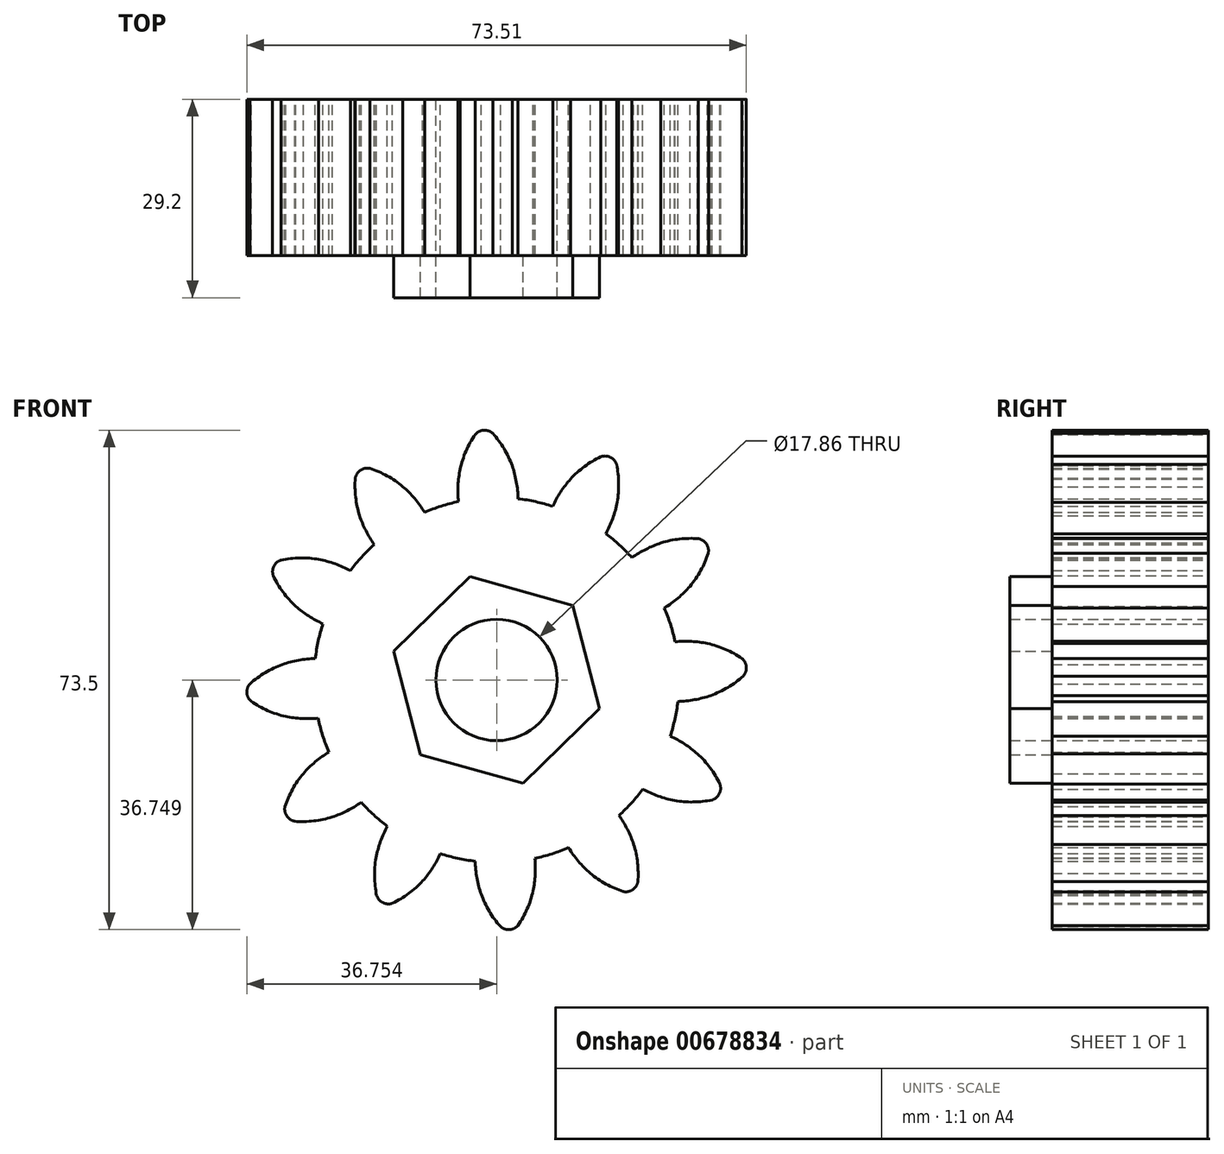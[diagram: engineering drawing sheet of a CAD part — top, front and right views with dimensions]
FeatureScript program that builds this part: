
annotation { "Feature Type Name" : "Feature", "Feature Type Description" : "" }
export const myFeature = defineFeature(function(context is Context, id is Id, definition is map)
    precondition{}
    {
        {
            var Q0;
            Q0=qCreatedBy(makeId("Front.planeOp"),FACE);
            var sketch = newSketch(context, id + "F0", { "sketchPlane" : qUnion([Q0])});
            skCircle(sketch, "E0", {"center": v(4.2, 11.54) * mm, "radius": 26.86 * mm});
            skCircle(sketch, "E1", {"center": v(4.2, 11.54) * mm, "radius": 29.34 * mm, "construction": true});
            skCircle(sketch, "E2", {"center": v(4.2, 11.54) * mm, "radius": 31.75 * mm, "construction": true});
            skLineSegment(sketch, "E3", {"start": v(4.2, 11.54) * mm, "end": v(4.2, 64.57) * mm, "construction": true});
            skLineSegment(sketch, "E4", {"start": v(4.2, 11.54) * mm, "end": v(-2.1, 107.57) * mm, "construction": true});
            skCircle(sketch, "E5", {"center": v(4.2, 11.54) * mm, "radius": 27.57 * mm, "construction": true});
            skLineSegment(sketch, "E6", {"start": v(4.2, 40.88) * mm, "end": v(-62.18, 40.88) * mm, "construction": true});
            skLineSegment(sketch, "E7", {"start": v(4.2, 40.88) * mm, "end": v(-57.88, 18.28) * mm, "construction": true});
            skCircle(sketch, "E8", {"center": v(4.2, 40.88) * mm, "radius": 14.6 * mm, "construction": true});
            skCircle(sketch, "E9", {"center": v(-9.53, 35.88) * mm, "radius": 14.6 * mm, "construction": true});
            skArc(sketch, "E10", {"start": v(6.48, 43.07) * mm, "mid": v(5.28, 45.59) * mm, "end": v(3.62, 47.83) * mm});
            skArc(sketch, "E11", {"start": v(7.36, 38.11) * mm, "mid": v(7.11, 40.63) * mm, "end": v(6.48, 43.07) * mm});
            skArc(sketch, "E12.MirrorCS", {"start": v(-1.18, 42.57) * mm, "mid": v(-0.31, 45.22) * mm, "end": v(1.03, 47.67) * mm});
            skArc(sketch, "E13.MirrorCS", {"start": v(-1.4, 37.54) * mm, "mid": v(-1.49, 40.06) * mm, "end": v(-1.18, 42.57) * mm});
            skArc(sketch, "E14", {"start": v(3.62, 47.83) * mm, "mid": v(2.3, 48.29) * mm, "end": v(1.03, 47.67) * mm});
            skCircle(sketch, "E15.cCircle", {"center": v(4.2, 11.54) * mm, "radius": 13.6 * mm, "construction": true});
            skLineSegment(sketch, "E15.0", {"start": v(15.43, 22.52) * mm, "end": v(19.32, 7.3) * mm});
            skLineSegment(sketch, "E15.1", {"start": v(19.32, 7.3) * mm, "end": v(8.09, -3.68) * mm});
            skLineSegment(sketch, "E15.2", {"start": v(8.09, -3.68) * mm, "end": v(-7.04, 0.56) * mm});
            skLineSegment(sketch, "E15.3", {"start": v(-7.04, 0.56) * mm, "end": v(-10.93, 15.78) * mm});
            skLineSegment(sketch, "E15.4", {"start": v(-10.93, 15.78) * mm, "end": v(0.3, 26.76) * mm});
            skLineSegment(sketch, "E15.5", {"start": v(0.3, 26.76) * mm, "end": v(15.43, 22.52) * mm});
            skPoint(sketch, "E15.0.midPoint", {"position": v(17.37, 14.9) * mm});
            skPoint(sketch, "E16.0.midPoint", {"position": v(11.4, 13.23) * mm});
            skCircle(sketch, "E17", {"center": v(4.2, 11.54) * mm, "radius": 8.93 * mm});
            skSolve(sketch);
        }
        {
            var Q0;
            {var subQ2=sQuery(id+"F0.wireOp",EDGE,"E10");Q0=makeQuery(id+"F0.imprint","IMPRINT",FACE,{"disambiguationData":[TD([[makeQuery(id+"F0.imprint","IMPRINT",EDGE,{"derivedFrom":subQ2}),1.0]])]});}
            var Q1;
            {var subQ0=sQuery(id+"F0.wireOp",EDGE,"E0");var subQ1=makeQuery(id+"F0.imprint","INTERSECT",VERTEX,{"derivedFrom":[subQ0,sQuery(id+"F0.wireOp",EDGE,"E11")]});Q1=makeQuery(id+"F0.imprint","IMPRINT",FACE,{"disambiguationData":[TD([[makeQuery(id+"F0.imprint","IMPRINT",EDGE,{"disambiguationData":[TD([[subQ1,-1.0]])],"derivedFrom":subQ0}),1.0]])]});}
            extrude(context, id + "F1", {"entities" : qUnion([Q0, Q1]), "depth" : 23 * mm, "offsetDistance" : 25 * mm});
        }
        {
            var Q0;
            Q0=makeQuery(id+"F1.opExtrude","SWEPT_BODY",BODY,{"disambiguationData":[OSD([sQuery(id+"F0.wireOp",EDGE,"E0"),sQuery(id+"F0.wireOp",EDGE,"E10"),sQuery(id+"F0.wireOp",EDGE,"E11"),sQuery(id+"F0.wireOp",EDGE,"E12.MirrorCS"),sQuery(id+"F0.wireOp",EDGE,"E13.MirrorCS"),sQuery(id+"F0.wireOp",EDGE,"E14")])]});
            var Q1;
            Q1=makeQuery(id+"F1.opExtrude","SWEPT_FACE",FACE,{"disambiguationData":[OSD([sQuery(id+"F0.wireOp",EDGE,"E0")])]});
            circularPattern(context, id + "F2", {"operationType" : NewBodyOperationType.ADD, "entities" : qUnion([Q0]), "axis" : qUnion([Q1]), "angle" : 360 * degree, "instanceCount" : 12, "equalSpace" : true});
        }
        {
            var Q0;
            Q0=makeQuery(id+"F0.imprint","IMPRINT",FACE,{"disambiguationData":[TD([[makeQuery(id+"F0.imprint","IMPRINT",EDGE,{"derivedFrom":sQuery(id+"F0.wireOp",EDGE,"E15.0")}),-1.0]])]});
            extrude(context, id + "F3", {"entities" : qUnion([Q0]), "operationType" : NewBodyOperationType.ADD, "depth" : 29.2 * mm, "offsetDistance" : 25 * mm});
        }
    });
